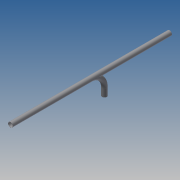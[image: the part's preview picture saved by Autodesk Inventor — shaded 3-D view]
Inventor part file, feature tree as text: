
AUTODESK INVENTOR PART (.ipt)
format: ipt  version: 2014 SP1 (Build 180222100, 222)  size: 181,760 bytes
history: native  units: in
note: dims shown in document units (in); Inventor stores cm internally (conversion verified against a paired STEP export)
features: sketch x5, extrude x3, plane x1, sweep x1
ambient origin geometry x8: Origin, YZ Plane, XZ Plane, XY Plane, X Axis, Y Axis, Z Axis, Center Point
bodies: Solid1 (feature_tree)
feature tree (10):
  extrude  "Extrusion1"  Depth=0.1in
  sketch  "Sketch4"  dims[d2=6.0in d3=0.0in d7=12.0in]
  plane  "Work Plane4"
  sweep  "Sweep1"
  extrude  "Extrusion2"  Depth=6.0in TaperAngle=0.0deg
  extrude  "Extrusion3"  [1 undecoded]
  sketch  "Sketch1"  dims[d0=3.937in d1=0.1in]
  sketch  "Sketch8"  dims[d9=0.0in d10=6.0in d11=0.0in]
  sketch  "Sketch9"  dims[d12=60.0in d13=72.0in d14=0.0in d15=0.0in]
  sketch  "Sketch10"
note: 1 required parameter value undecoded (feature->parameter linkage not recoverable at this tier; creation-order binding heuristic only, values carry confidence <= 0.55)
